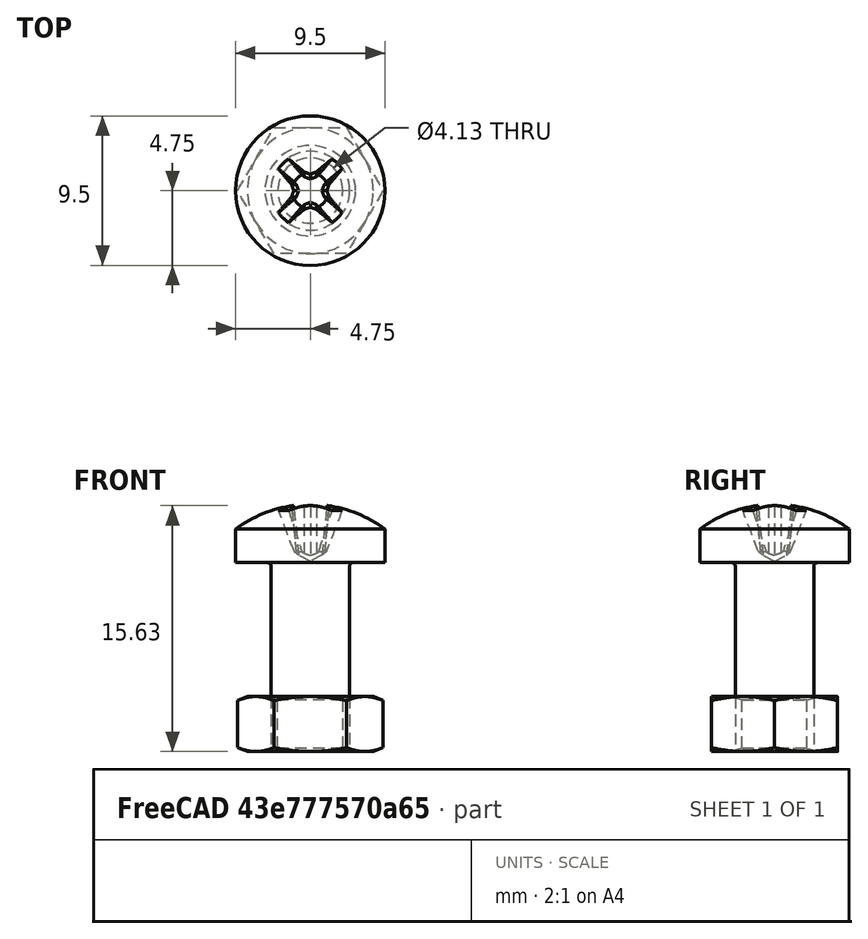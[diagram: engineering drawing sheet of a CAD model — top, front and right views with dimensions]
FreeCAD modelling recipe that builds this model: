
FCSTD DOCUMENT  (FreeCAD 0.21R33771 (Git))
Label: assembly
License: All rights reserved
LicenseURL: http://en.wikipedia.org/wiki/All_rights_reserved
objects: App::DocumentObjectGroup×3, App::Link×3, Part::FeaturePython×2, PartDesign::CoordinateSystem×1, App::FeaturePython×1, App::Part×1
note: 3 computed .brp shape members not serialized (recipe doc carries the construction recipe); baked Part::Feature solids carry a one-line shape summary decoded from their .brp
EXTERNAL_REF file=clip.FCStd obj=HoleAxis_1
EXTERNAL_REF file=clip.FCStd obj=Body
EXTERNAL_REF file=rectangle.FCStd obj=HoleAxis_1
EXTERNAL_REF file=rectangle.FCStd obj=Part

FEATURE [App::DocumentObjectGroup] Parts
FEATURE [PartDesign::CoordinateSystem] LCS_Origin
  AttacherType = Attacher::AttachEngine3D
  MapMode = 2
  Support = -> [X_Axis]
FEATURE [App::DocumentObjectGroup] Constraints
FEATURE [App::FeaturePython] Variables  # WARN: FeaturePython — macro-defined, semantics opaque (R4)
  Type = App::PropertyContainer
FEATURE [App::DocumentObjectGroup] Configurations
FEATURE [App::Link] clip
  AttachedBy = #HoleAxis_1
  AttachedTo = Parent Assembly#LCS_Origin
  LinkPlacement = pos=(-35,-5,-3) rot=(0,0,-1;3.14159rad)
  LinkedObject = -> <external clip.FCStd>#Body
  Placement = pos=(-35,-5,-3) rot=(0,0,-1;3.14159rad)
  SolverId = Asm4EE
  expr: Placement = LCS_Origin.Placement * AttachmentOffset * clip#HoleAxis_1.Placement ^ -1
FEATURE [Part::FeaturePython] Screw  label="M5x12-Screw"  # WARN: FeaturePython — macro-defined, semantics opaque (R4)
  Diameter = 7
  Invert = false
  LeftHanded = false
  Length = 3
  LengthCustom = 12
  MatchOuter = false
  OffsetAngle = 0
  Thread = false
  Type = 76
FEATURE [App::Link] rectangle
  AttachedBy = #HoleAxis_1
  AttachedTo = clip#HoleAxis_1
  AttachmentOffset = pos=(0,0,-3) rot=(0,0,1;0rad)
  LinkPlacement = pos=(35,7e-15,-6) rot=(0,0,1;0rad)
  LinkedObject = -> <external rectangle.FCStd>#Part
  Placement = pos=(35,7e-15,-6) rot=(0,0,1;0rad)
  SolverId = Asm4EE
  expr: Placement = clip.Placement * clip#HoleAxis_1.Placement * AttachmentOffset * rectangle#HoleAxis_1.Placement ^ -1
FEATURE [Part::FeaturePython] Nut  label="M5-Nut"  # WARN: FeaturePython — macro-defined, semantics opaque (R4)
  AttachedBy = Origin
  AttachedTo = clip#HoleAxis_1
  AttachmentOffset = pos=(0,0,-12) rot=(0,0,1;0rad)
  Diameter = 7
  Invert = false
  LeftHanded = false
  MatchOuter = false
  OffsetAngle = 0
  Placement = pos=(0,2.7e-15,-12) rot=(0,0,1;0rad)
  SolverId = Asm4EE
  Thread = false
  Type = 31
  expr: Placement = clip.Placement * clip#HoleAxis_1.Placement * AttachmentOffset
FEATURE [App::Link] Body
  AttachedBy = #HoleAxis_1
  AttachedTo = clip#HoleAxis_1
  AttachmentOffset = pos=(0,0,-9) rot=(1,0,0;3.14159rad)
  LinkPlacement = pos=(-35,5,-6) rot=(0,1,0;3.14159rad)
  LinkedObject = -> <external clip.FCStd>#Body
  Placement = pos=(-35,5,-6) rot=(0,1,0;3.14159rad)
  SolverId = Asm4EE
  expr: Placement = clip.Placement * clip#HoleAxis_1.Placement * AttachmentOffset * clip#HoleAxis_1.Placement ^ -1
FEATURE [App::Part] Assembly
  AssemblyType = Part::Link
  Group = -> [LCS_Origin,Constraints,Variables,Configurations,clip,rectangle,Nut,Body]
  Origin = -> Origin
  Type = Assembly

RESOLVED EXTERNAL PARTS (link-assembly join: the EXTERNAL_REF files above that resolve inside this repo's crawl, each included once):
---- part clip.FCStd = doc fcstd_2fc916cb0d59 ----
FCSTD DOCUMENT  (FreeCAD 0.21R33771 (Git))
Label: clip
License: All rights reserved
LicenseURL: http://en.wikipedia.org/wiki/All_rights_reserved
objects: Sketcher::SketchObject×2, PartDesign::Pad×1, PartDesign::Pocket×1, PartDesign::CoordinateSystem×1, PartDesign::Line×1, PartDesign::Body×1
note: 9 computed .brp shape members not serialized (recipe doc carries the construction recipe); baked Part::Feature solids carry a one-line shape summary decoded from their .brp

FEATURE [Sketcher::SketchObject] Sketch
  FullyConstrained = true
  MapMode = 5
  Placement = pos=(0,0,0) rot=(1,0,0;1.5708rad)
  Support = -> [XZ_Plane]
  sketch-geometry (10):
    g0: ArcOfCircle CenterX=0 CenterY=0 CenterZ=0 NormalX=0 NormalY=0 NormalZ=1 AngleXU=0 Radius=30.1496 StartAngle=0.0996687 EndAngle=3.04192
    g1: LineSegment StartX=-30 StartY=3 StartZ=0 EndX=-40 EndY=3 EndZ=0
    g2: LineSegment StartX=-40 StartY=3 StartZ=0 EndX=-40 EndY=0 EndZ=0
    g3: LineSegment StartX=-40 StartY=0 StartZ=0 EndX=-27 EndY=0 EndZ=0
    g4: LineSegment StartX=40 StartY=0 StartZ=0 EndX=40 EndY=3 EndZ=0
    g5: LineSegment StartX=40 StartY=3 StartZ=0 EndX=30 EndY=3 EndZ=0
    g6: ArcOfCircle CenterX=0 CenterY=0 CenterZ=0 NormalX=0 NormalY=0 NormalZ=1 AngleXU=0 Radius=27.1662 StartAngle=0.110657 EndAngle=3.03094
    g7: LineSegment StartX=-27 StartY=3 StartZ=0 EndX=-27 EndY=0 EndZ=0
    g8: LineSegment StartX=27 StartY=3 StartZ=0 EndX=27 EndY=0 EndZ=0
    g9: LineSegment StartX=27 StartY=0 StartZ=0 EndX=40 EndY=0 EndZ=0
  constraints (30):
    c: Coincident(g0,g1)
    c: Coincident(g1,g2)
    c: PointOnObject(g2,g-1)
    c: Vertical(g2)
    c: Coincident(g2,g3)
    c: PointOnObject(g9,g-1)
    c: Coincident(g9,g4)
    c: Coincident(g4,g5)
    c: Coincident(g5,g0)
    c: Horizontal(g1)
    c: Horizontal(g5)
    c: Vertical(g4)
    c: Equal(g1,g5)
    c: Equal(g4,g2)
    c: DistanceX(g3,g9) = 80
    c: DistanceX(g5,g5) = 10
    c: DistanceY(g4,g4) = 3
    c: Coincident(g0,g-1)
    c: Coincident(g7,g6)
    c: Vertical(g7)
    c: Coincident(g8,g6)
    c: Horizontal(g0,g6)
    c: Horizontal(g6,g6)
    c: Vertical(g8)
    c: DistanceX(g6,g0) = 3
    c: Coincident(g6,g0)
    c: Coincident(g3,g7)
    c: Coincident(g9,g8)
    c: PointOnObject(g3,g-1)
    c: Equal(g3,g9)
FEATURE [PartDesign::Pad] Pad
  Direction = (0,-1,2e-16)
  Length = 10
  Length2 = 10
  Placement = pos=(0,0,0) rot=(1,0,0;1.5708rad)
  Profile = -> Sketch
  ReferenceAxis = -> Sketch [N_Axis]
  Type = 0
FEATURE [Sketcher::SketchObject] Sketch001
  ExternalGeometry = -> [Pad]
  FullyConstrained = true
  MapMode = 5
  Placement = pos=(0,2e-15,3) rot=(0,0,1;3.14159rad)
  Support = -> [Pad]
  sketch-geometry (2):
    g0: Circle CenterX=-35 CenterY=5 CenterZ=0 NormalX=0 NormalY=0 NormalZ=1 AngleXU=0 Radius=2.5
    g1: Circle CenterX=35 CenterY=5 CenterZ=0 NormalX=0 NormalY=0 NormalZ=1 AngleXU=0 Radius=2.5
  constraints (4):
    c: Diameter(g0) = 5
    c: Diameter(g1) = 5
    c: Symmetric(g-3,g-4,g0)
    c: Symmetric(g-6,g-5,g1)
FEATURE [PartDesign::Pocket] Pocket
  BaseFeature = -> Pad
  Direction = (0,-2e-16,-1)
  Length = 3
  Length2 = 5
  Placement = pos=(0,0,0) rot=(1,0,0;1.5708rad)
  Profile = -> Sketch001
  ReferenceAxis = -> Sketch001 [N_Axis]
  Type = 0
FEATURE [PartDesign::CoordinateSystem] LCS_origin
  AttacherType = Attacher::AttachEngine3D
FEATURE [PartDesign::Line] HoleAxis_1
  AttacherType = Attacher::AttachEngineLine
  Length = 7.04534
  MapMode = 19
  Placement = pos=(-35,-5,3) rot=(0,0,1;3.14159rad)
  ResizeMode = 1
  Support = -> [Pocket]
FEATURE [PartDesign::Body] Body
  Group = -> [Sketch,Pad,Sketch001,Pocket,LCS_origin,HoleAxis_1]
  Origin = -> Origin
  Tip = -> Pocket
---- part rectangle.FCStd = doc fcstd_d251a489c5ca ----
FCSTD DOCUMENT  (FreeCAD 0.21R33771 (Git))
Label: rectangle
License: All rights reserved
LicenseURL: http://en.wikipedia.org/wiki/All_rights_reserved
objects: Sketcher::SketchObject×1, Part::Extrusion×1, PartDesign::Line×1, App::Part×1
note: 3 computed .brp shape members not serialized (recipe doc carries the construction recipe); baked Part::Feature solids carry a one-line shape summary decoded from their .brp

FEATURE [Sketcher::SketchObject] Sketch
  FullyConstrained = true
  sketch-geometry (5):
    g0: LineSegment StartX=-40 StartY=6 StartZ=0 EndX=40 EndY=6 EndZ=0
    g1: LineSegment StartX=40 StartY=6 StartZ=0 EndX=40 EndY=-6 EndZ=0
    g2: LineSegment StartX=40 StartY=-6 StartZ=0 EndX=-40 EndY=-6 EndZ=0
    g3: LineSegment StartX=-40 StartY=-6 StartZ=0 EndX=-40 EndY=6 EndZ=0
    g4: Circle CenterX=-35 CenterY=0 CenterZ=0 NormalX=0 NormalY=0 NormalZ=1 AngleXU=0 Radius=2.5
  constraints (14):
    c: Coincident(g0,g1)
    c: Coincident(g1,g2)
    c: Coincident(g2,g3)
    c: Coincident(g3,g0)
    c: Horizontal(g0)
    c: Horizontal(g2)
    c: Vertical(g1)
    c: Vertical(g3)
    c: Symmetric(g2,g0,g-1)
    c: DistanceX(g0,g0) = 80
    c: DistanceY(g1,g1) = 12
    c: PointOnObject(g4,g-1)
    c: Diameter(g4) = 5
    c: DistanceX(g0,g4) = 5
FEATURE [Part::Extrusion] Extrude
  Base = -> Sketch
  Dir = (0,0,1)
  DirMode = 2
  FaceMakerClass = Part::FaceMakerBullseye
  LengthFwd = 3
  LengthRev = 0
  Solid = true
  Symmetric = false
FEATURE [PartDesign::Line] HoleAxis_1
  AttacherType = Attacher::AttachEngineLine
  Length = 7.04534
  MapMode = 19
  Placement = pos=(-35,0,3) rot=(0,0,1;0rad)
  ResizeMode = 1
  Support = -> [Extrude]
FEATURE [App::Part] Part  label="rectangle"
  Group = -> [Sketch,Extrude,HoleAxis_1]
  Origin = -> Origin
